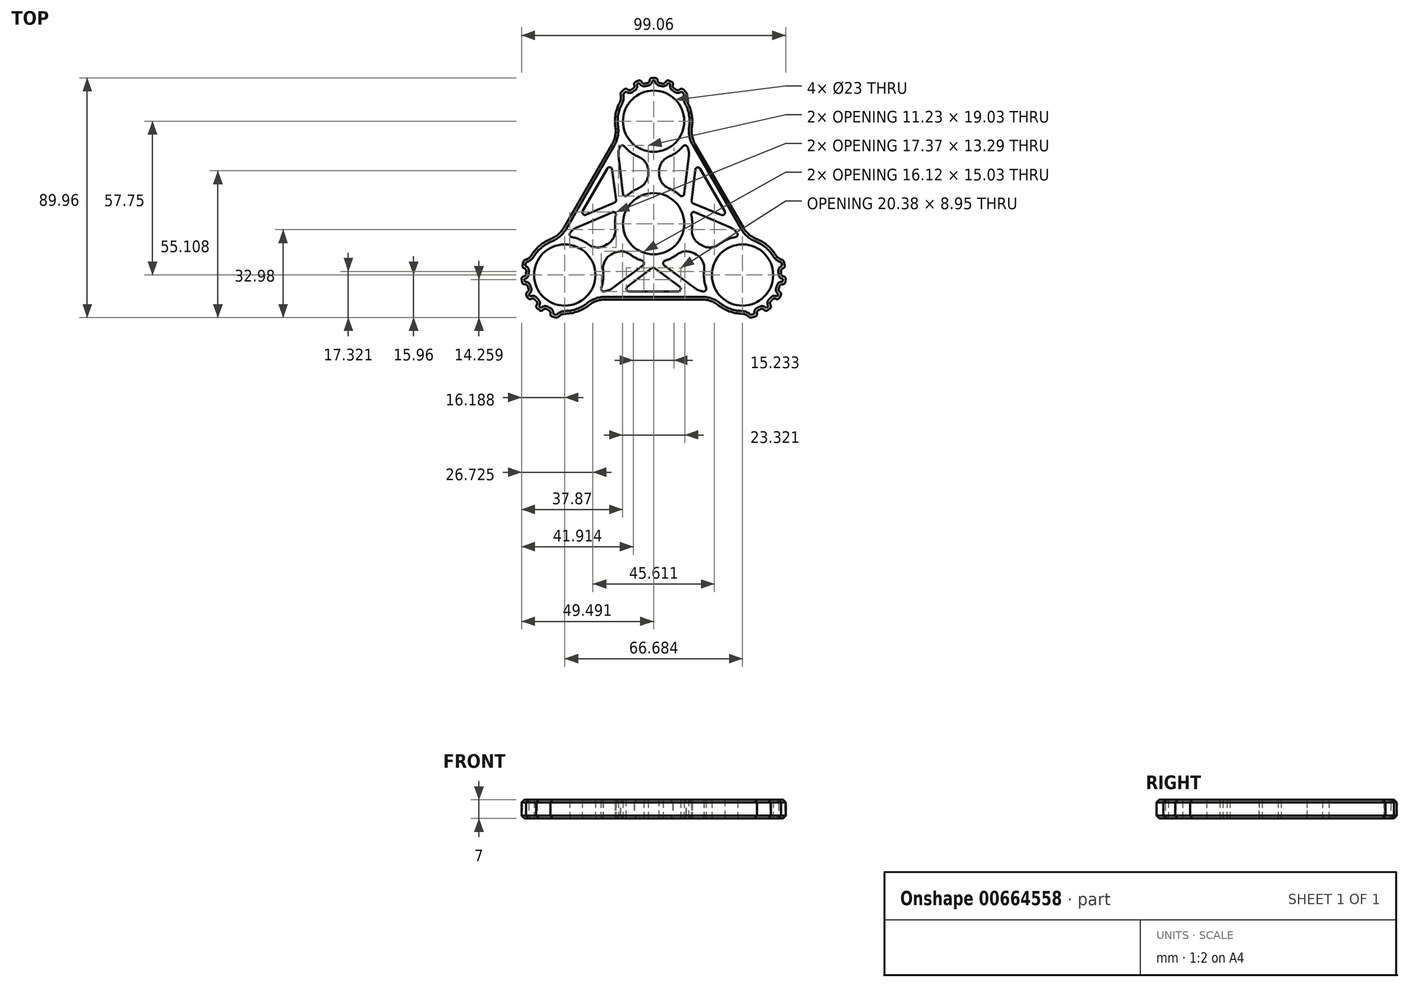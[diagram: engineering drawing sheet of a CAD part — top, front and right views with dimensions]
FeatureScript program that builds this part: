
annotation { "Feature Type Name" : "Feature", "Feature Type Description" : "" }
export const myFeature = defineFeature(function(context is Context, id is Id, definition is map)
    precondition{}
    {
        {
            var Q0;
            Q0=qCreatedBy(makeId("Top.planeOp"),FACE);
            var sketch = newSketch(context, id + "F0", { "sketchPlane" : qUnion([Q0])});
            skCircle(sketch, "E0", {"center": v(0, 0) * mm, "radius": 11.5 * mm});
            skArc(sketch, "E1.0", {"start": v(-2, 14.36) * mm, "mid": v(-7.13, 12.63) * mm, "end": v(-11.27, 9.13) * mm});
            skCircle(sketch, "E2", {"center": v(0, 38.5) * mm, "radius": 11.5 * mm});
            skArc(sketch, "E3.0", {"start": v(-11.26, 47.64) * mm, "mid": v(-14.31, 40.8) * mm, "end": v(-13.56, 33.37) * mm});
            skLineSegment(sketch, "E4", {"start": v(0, 11.5) * mm, "end": v(0, 27) * mm, "construction": true});
            skLineSegment(sketch, "E5.0", {"start": v(2, 14.36) * mm, "end": v(2, 24.14) * mm});
            skLineSegment(sketch, "E6.0", {"start": v(-2, 14.36) * mm, "end": v(-2, 24.14) * mm});
            skLineSegment(sketch, "E7", {"start": v(0, 53) * mm, "end": v(0, 55) * mm, "construction": true});
            skLineSegment(sketch, "E8.0", {"start": v(1.5, 52.92) * mm, "end": v(1.5, 54.75) * mm});
            skLineSegment(sketch, "E9.0", {"start": v(-1.5, 52.92) * mm, "end": v(-1.5, 54.75) * mm});
            skLineSegment(sketch, "E10", {"start": v(-1.5, 54.75) * mm, "end": v(1.5, 54.75) * mm});
            skLineSegment(sketch, "E11.1.0", {"start": v(4.83, 54.09) * mm, "end": v(7.6, 52.94) * mm});
            skLineSegment(sketch, "E11.1.1", {"start": v(4.13, 52.4) * mm, "end": v(4.83, 54.09) * mm});
            skLineSegment(sketch, "E11.1.2", {"start": v(6.9, 51.25) * mm, "end": v(7.6, 52.94) * mm});
            skLineSegment(sketch, "E11.2.0", {"start": v(10.43, 51.05) * mm, "end": v(12.55, 48.93) * mm});
            skLineSegment(sketch, "E11.2.1", {"start": v(9.14, 49.76) * mm, "end": v(10.43, 51.05) * mm});
            skLineSegment(sketch, "E11.2.2", {"start": v(11.26, 47.64) * mm, "end": v(12.55, 48.93) * mm});
            skLineSegment(sketch, "E11.anchor1", {"start": v(0, 38.5) * mm, "end": v(-1.5, 54.75) * mm, "construction": true});
            skLineSegment(sketch, "E11.anchor2", {"start": v(0, 38.5) * mm, "end": v(10.43, 51.05) * mm, "construction": true});
            skLineSegment(sketch, "E12.MirrorCS", {"start": v(-4.83, 54.09) * mm, "end": v(-7.6, 52.94) * mm});
            skLineSegment(sketch, "E13.MirrorCS", {"start": v(-4.13, 52.4) * mm, "end": v(-4.83, 54.09) * mm});
            skLineSegment(sketch, "E14.MirrorCS", {"start": v(-6.9, 51.25) * mm, "end": v(-7.6, 52.94) * mm});
            skLineSegment(sketch, "E15.MirrorCS", {"start": v(-9.14, 49.76) * mm, "end": v(-10.43, 51.05) * mm});
            skLineSegment(sketch, "E16.MirrorCS", {"start": v(-10.43, 51.05) * mm, "end": v(-12.55, 48.93) * mm});
            skLineSegment(sketch, "E17.MirrorCS", {"start": v(-11.26, 47.64) * mm, "end": v(-12.55, 48.93) * mm});
            skArc(sketch, "E18.trimOffspring", {"start": v(-6.9, 51.25) * mm, "mid": v(-8.06, 50.56) * mm, "end": v(-9.14, 49.76) * mm});
            skArc(sketch, "E19.trimOffspring", {"start": v(-1.33, 52.94) * mm, "mid": v(-2.75, 52.74) * mm, "end": v(-4.13, 52.4) * mm});
            skArc(sketch, "E20.trimOffspring", {"start": v(4.13, 52.4) * mm, "mid": v(2.83, 52.72) * mm, "end": v(1.5, 52.92) * mm});
            skArc(sketch, "E21.trimOffspring", {"start": v(9.27, 49.65) * mm, "mid": v(8.13, 50.5) * mm, "end": v(6.9, 51.25) * mm});
            skArc(sketch, "E22.trimOffspring", {"start": v(2, 24.14) * mm, "mid": v(7.6, 26.15) * mm, "end": v(11.9, 30.23) * mm});
            skLineSegment(sketch, "E23.1.0", {"start": v(-33.34, -19.25) * mm, "end": v(-46.66, -28.67) * mm, "construction": true});
            skPoint(sketch, "E23.1.1", {"position": v(-33.34, -19.25) * mm});
            skCircle(sketch, "E23.1.2", {"center": v(-33.34, -19.25) * mm, "radius": 11.5 * mm});
            skLineSegment(sketch, "E23.1.3", {"start": v(-9.96, -5.75) * mm, "end": v(-23.38, -13.5) * mm, "construction": true});
            skArc(sketch, "E23.1.4", {"start": v(-35.63, -33.57) * mm, "mid": v(-28.18, -32.8) * mm, "end": v(-22.12, -28.43) * mm});
            skLineSegment(sketch, "E23.1.5", {"start": v(-13.44, -5.45) * mm, "end": v(-21.9, -10.34) * mm});
            skLineSegment(sketch, "E23.1.6", {"start": v(-11.44, -8.91) * mm, "end": v(-19.9, -13.8) * mm});
            skLineSegment(sketch, "E23.1.7", {"start": v(-33.34, -19.25) * mm, "end": v(-49.43, -16.5) * mm, "construction": true});
            skArc(sketch, "E23.1.8", {"start": v(-21.9, -10.34) * mm, "mid": v(-26.44, -6.5) * mm, "end": v(-32.13, -4.8) * mm});
            skLineSegment(sketch, "E23.1.9", {"start": v(-40.93, -31.6) * mm, "end": v(-42.04, -33.06) * mm});
            skLineSegment(sketch, "E23.1.10", {"start": v(-35.63, -33.57) * mm, "end": v(-36.1, -35.33) * mm});
            skLineSegment(sketch, "E23.1.11", {"start": v(-49.43, -16.5) * mm, "end": v(-48.65, -13.6) * mm});
            skLineSegment(sketch, "E23.1.12", {"start": v(-47.84, -19.65) * mm, "end": v(-49.65, -19.88) * mm});
            skArc(sketch, "E23.1.13", {"start": v(-47.63, -16.8) * mm, "mid": v(-47.8, -18.22) * mm, "end": v(-47.84, -19.65) * mm});
            skLineSegment(sketch, "E23.1.14", {"start": v(-44.42, -31.23) * mm, "end": v(-42.04, -33.06) * mm});
            skLineSegment(sketch, "E23.1.15", {"start": v(-45.9, -26.5) * mm, "end": v(-47.63, -27.5) * mm, "construction": true});
            skLineSegment(sketch, "E23.1.16", {"start": v(-46.58, -25.16) * mm, "end": v(-48.16, -26.08) * mm});
            skLineSegment(sketch, "E23.1.17", {"start": v(-46.66, -28.67) * mm, "end": v(-48.16, -26.08) * mm});
            skLineSegment(sketch, "E23.1.18", {"start": v(-45.08, -27.76) * mm, "end": v(-46.66, -28.67) * mm});
            skLineSegment(sketch, "E23.1.19", {"start": v(-49.26, -22.86) * mm, "end": v(-49.65, -19.88) * mm});
            skLineSegment(sketch, "E23.1.20", {"start": v(-47.45, -22.62) * mm, "end": v(-49.26, -22.86) * mm});
            skArc(sketch, "E23.1.21", {"start": v(-47.45, -22.62) * mm, "mid": v(-47.07, -23.91) * mm, "end": v(-46.58, -25.16) * mm});
            skArc(sketch, "E23.1.22", {"start": v(-40.93, -31.6) * mm, "mid": v(-39.76, -32.25) * mm, "end": v(-38.52, -32.8) * mm});
            skLineSegment(sketch, "E23.1.23", {"start": v(-39, -34.56) * mm, "end": v(-36.1, -35.33) * mm});
            skLineSegment(sketch, "E23.1.24", {"start": v(-43.31, -29.78) * mm, "end": v(-44.42, -31.23) * mm});
            skLineSegment(sketch, "E23.1.25", {"start": v(-46.88, -14.07) * mm, "end": v(-48.65, -13.6) * mm});
            skArc(sketch, "E23.1.26", {"start": v(-45.18, -27.62) * mm, "mid": v(-44.3, -28.75) * mm, "end": v(-43.31, -29.78) * mm});
            skLineSegment(sketch, "E23.1.27", {"start": v(-38.52, -32.8) * mm, "end": v(-39, -34.56) * mm});
            skLineSegment(sketch, "E23.1.28", {"start": v(-47.66, -16.97) * mm, "end": v(-49.43, -16.5) * mm});
            skLineSegment(sketch, "E23.2.0", {"start": v(33.34, -19.25) * mm, "end": v(48.16, -26.08) * mm, "construction": true});
            skPoint(sketch, "E23.2.1", {"position": v(33.34, -19.25) * mm});
            skCircle(sketch, "E23.2.2", {"center": v(33.34, -19.25) * mm, "radius": 11.5 * mm});
            skLineSegment(sketch, "E23.2.3", {"start": v(9.96, -5.75) * mm, "end": v(23.38, -13.5) * mm, "construction": true});
            skArc(sketch, "E23.2.4", {"start": v(46.88, -14.07) * mm, "mid": v(42.5, -8) * mm, "end": v(35.68, -4.94) * mm});
            skLineSegment(sketch, "E23.2.5", {"start": v(11.44, -8.91) * mm, "end": v(19.9, -13.8) * mm});
            skLineSegment(sketch, "E23.2.6", {"start": v(13.44, -5.45) * mm, "end": v(21.9, -10.34) * mm});
            skLineSegment(sketch, "E23.2.7", {"start": v(33.34, -19.25) * mm, "end": v(39, -34.56) * mm, "construction": true});
            skArc(sketch, "E23.2.8", {"start": v(19.9, -13.8) * mm, "mid": v(18.85, -19.65) * mm, "end": v(20.22, -25.43) * mm});
            skLineSegment(sketch, "E23.2.9", {"start": v(47.84, -19.65) * mm, "end": v(49.65, -19.88) * mm});
            skLineSegment(sketch, "E23.2.10", {"start": v(46.88, -14.07) * mm, "end": v(48.65, -13.6) * mm});
            skLineSegment(sketch, "E23.2.11", {"start": v(39, -34.56) * mm, "end": v(36.1, -35.33) * mm});
            skLineSegment(sketch, "E23.2.12", {"start": v(40.93, -31.6) * mm, "end": v(42.04, -33.06) * mm});
            skArc(sketch, "E23.2.13", {"start": v(38.37, -32.85) * mm, "mid": v(39.68, -32.3) * mm, "end": v(40.93, -31.6) * mm});
            skLineSegment(sketch, "E23.2.14", {"start": v(49.26, -22.86) * mm, "end": v(49.65, -19.88) * mm});
            skLineSegment(sketch, "E23.2.15", {"start": v(45.9, -26.5) * mm, "end": v(47.63, -27.5) * mm, "construction": true});
            skLineSegment(sketch, "E23.2.16", {"start": v(45.08, -27.76) * mm, "end": v(46.66, -28.67) * mm});
            skLineSegment(sketch, "E23.2.17", {"start": v(48.16, -26.08) * mm, "end": v(46.66, -28.67) * mm});
            skLineSegment(sketch, "E23.2.18", {"start": v(46.58, -25.16) * mm, "end": v(48.16, -26.08) * mm});
            skLineSegment(sketch, "E23.2.19", {"start": v(44.42, -31.23) * mm, "end": v(42.04, -33.06) * mm});
            skLineSegment(sketch, "E23.2.20", {"start": v(43.31, -29.78) * mm, "end": v(44.42, -31.23) * mm});
            skArc(sketch, "E23.2.21", {"start": v(43.31, -29.78) * mm, "mid": v(44.24, -28.81) * mm, "end": v(45.08, -27.76) * mm});
            skArc(sketch, "E23.2.22", {"start": v(47.84, -19.65) * mm, "mid": v(47.81, -18.3) * mm, "end": v(47.66, -16.97) * mm});
            skLineSegment(sketch, "E23.2.23", {"start": v(49.43, -16.5) * mm, "end": v(48.65, -13.6) * mm});
            skLineSegment(sketch, "E23.2.24", {"start": v(47.45, -22.62) * mm, "end": v(49.26, -22.86) * mm});
            skLineSegment(sketch, "E23.2.25", {"start": v(35.63, -33.57) * mm, "end": v(36.1, -35.33) * mm});
            skArc(sketch, "E23.2.26", {"start": v(46.51, -25.32) * mm, "mid": v(47.05, -24) * mm, "end": v(47.45, -22.62) * mm});
            skLineSegment(sketch, "E23.2.27", {"start": v(47.66, -16.97) * mm, "end": v(49.43, -16.5) * mm});
            skLineSegment(sketch, "E23.2.28", {"start": v(38.52, -32.8) * mm, "end": v(39, -34.56) * mm});
            skArc(sketch, "E24.trimOffspring", {"start": v(13.44, -5.45) * mm, "mid": v(14.5, -0.14) * mm, "end": v(13.54, 5.2) * mm});
            skArc(sketch, "E25.trimOffspring", {"start": v(-11.44, -8.91) * mm, "mid": v(-7.37, -12.49) * mm, "end": v(-2.27, -14.32) * mm});
            skLineSegment(sketch, "E26", {"start": v(-13.56, 33.37) * mm, "end": v(-35.68, -4.94) * mm});
            skLineSegment(sketch, "E27.0", {"start": v(-11.9, 30.23) * mm, "end": v(-13.42, 27.6) * mm});
            skArc(sketch, "E28.trimOffspring", {"start": v(-11.9, 30.23) * mm, "mid": v(-7.6, 26.15) * mm, "end": v(-2, 24.14) * mm});
            skArc(sketch, "E29.trimOffspring", {"start": v(-35.68, -4.94) * mm, "mid": v(-42.5, -8) * mm, "end": v(-46.88, -14.07) * mm});
            skLineSegment(sketch, "E30", {"start": v(-12.56, 7.25) * mm, "end": v(-29.36, 0) * mm, "construction": true});
            skLineSegment(sketch, "E31", {"start": v(-12.56, 7.25) * mm, "end": v(-22.02, 12.71) * mm, "construction": true});
            skLineSegment(sketch, "E32.0", {"start": v(-13.95, 8.28) * mm, "end": v(-28.1, 2.18) * mm});
            skLineSegment(sketch, "E33.0", {"start": v(-13.54, 5.2) * mm, "end": v(-30.62, -2.18) * mm});
            skLineSegment(sketch, "E34.trimOffspring", {"start": v(-30.62, -2.18) * mm, "end": v(-32.13, -4.8) * mm});
            skArc(sketch, "E35.trimOffspring", {"start": v(-13.54, 5.2) * mm, "mid": v(-14.5, -0.14) * mm, "end": v(-13.44, -5.45) * mm});
            skLineSegment(sketch, "E36.MirrorCS", {"start": v(-11.27, 9.13) * mm, "end": v(-13.42, 27.6) * mm});
            skLineSegment(sketch, "E37.trimOffspring", {"start": v(-15.94, 23.25) * mm, "end": v(-28.1, 2.18) * mm});
            skPoint(sketch, "E38.orphan", {"position": v(-10.85, 9.62) * mm});
            skLineSegment(sketch, "E39.trimOffspring", {"start": v(-13.95, 8.28) * mm, "end": v(-15.94, 23.25) * mm});
            skPoint(sketch, "E40.MirrorCS.start.orphan", {"position": v(-13.76, 4.58) * mm});
            skLineSegment(sketch, "E41.1.0", {"start": v(-22.12, -28.43) * mm, "end": v(22.12, -28.43) * mm});
            skLineSegment(sketch, "E41.1.1", {"start": v(-0.2, -16.22) * mm, "end": v(-12.17, -25.43) * mm});
            skLineSegment(sketch, "E41.1.2", {"start": v(0, -14.5) * mm, "end": v(0, -25.43) * mm, "construction": true});
            skLineSegment(sketch, "E41.1.3", {"start": v(-12.17, -25.43) * mm, "end": v(12.17, -25.43) * mm});
            skLineSegment(sketch, "E41.1.4", {"start": v(-2.27, -14.32) * mm, "end": v(-17.2, -25.43) * mm});
            skLineSegment(sketch, "E41.1.5", {"start": v(17.2, -25.43) * mm, "end": v(20.22, -25.43) * mm});
            skLineSegment(sketch, "E41.1.6", {"start": v(2.27, -14.32) * mm, "end": v(17.2, -25.43) * mm});
            skLineSegment(sketch, "E41.1.7", {"start": v(-0.2, -16.22) * mm, "end": v(12.17, -25.43) * mm});
            skLineSegment(sketch, "E41.1.8", {"start": v(0, -14.5) * mm, "end": v(14.68, -25.43) * mm, "construction": true});
            skLineSegment(sketch, "E41.1.9", {"start": v(-20.22, -25.43) * mm, "end": v(-17.2, -25.43) * mm});
            skLineSegment(sketch, "E41.2.0", {"start": v(35.68, -4.94) * mm, "end": v(13.56, 33.37) * mm});
            skLineSegment(sketch, "E41.2.1", {"start": v(14.15, 7.94) * mm, "end": v(28.1, 2.18) * mm});
            skLineSegment(sketch, "E41.2.2", {"start": v(12.56, 7.25) * mm, "end": v(22.02, 12.71) * mm, "construction": true});
            skLineSegment(sketch, "E41.2.3", {"start": v(28.1, 2.18) * mm, "end": v(15.94, 23.25) * mm});
            skLineSegment(sketch, "E41.2.4", {"start": v(13.54, 5.2) * mm, "end": v(30.62, -2.18) * mm});
            skLineSegment(sketch, "E41.2.5", {"start": v(13.42, 27.6) * mm, "end": v(11.9, 30.23) * mm});
            skLineSegment(sketch, "E41.2.6", {"start": v(11.27, 9.13) * mm, "end": v(13.42, 27.6) * mm});
            skLineSegment(sketch, "E41.2.7", {"start": v(14.15, 7.94) * mm, "end": v(15.94, 23.25) * mm});
            skLineSegment(sketch, "E41.2.8", {"start": v(12.56, 7.25) * mm, "end": v(14.68, 25.43) * mm, "construction": true});
            skLineSegment(sketch, "E41.2.9", {"start": v(32.13, -4.8) * mm, "end": v(30.62, -2.18) * mm});
            skArc(sketch, "E42.trimOffspring", {"start": v(13.56, 33.37) * mm, "mid": v(14.31, 40.8) * mm, "end": v(11.26, 47.64) * mm});
            skArc(sketch, "E43.trimOffspring", {"start": v(32.13, -4.8) * mm, "mid": v(26.44, -6.5) * mm, "end": v(21.9, -10.34) * mm});
            skArc(sketch, "E44.trimOffspring", {"start": v(11.27, 9.13) * mm, "mid": v(7.13, 12.63) * mm, "end": v(2, 14.36) * mm});
            skArc(sketch, "E45.trimOffspring", {"start": v(2.27, -14.32) * mm, "mid": v(7.37, -12.49) * mm, "end": v(11.44, -8.91) * mm});
            skArc(sketch, "E46.trimOffspring", {"start": v(22.12, -28.43) * mm, "mid": v(28.18, -32.8) * mm, "end": v(35.63, -33.57) * mm});
            skArc(sketch, "E47.trimOffspring", {"start": v(-20.22, -25.43) * mm, "mid": v(-18.85, -19.65) * mm, "end": v(-19.9, -13.8) * mm});
            skSolve(sketch);
        }
        {
            var Q0;
            Q0=qSketchRegion(id+"F0",true);
            extrude(context, id + "F1", {"entities" : qUnion([Q0]), "depth" : 7 * mm});
        }
        {
            var Q0;
            Q0=makeQuery(id+"F1.opExtrude","SWEPT_EDGE",EDGE,{"disambiguationData":[OSD([sQuery(id+"F0.wireOp",EDGE,"E1.0"),sQuery(id+"F0.wireOp",EDGE,"E6.0")])]});
            var Q1;
            Q1=makeQuery(id+"F1.opExtrude","SWEPT_EDGE",EDGE,{"disambiguationData":[OSD([sQuery(id+"F0.wireOp",EDGE,"E5.0"),sQuery(id+"F0.wireOp",EDGE,"E44.trimOffspring")])]});
            var Q2;
            Q2=makeQuery(id+"F1.opExtrude","SWEPT_EDGE",EDGE,{"disambiguationData":[OSD([sQuery(id+"F0.wireOp",EDGE,"E5.0"),sQuery(id+"F0.wireOp",EDGE,"E22.trimOffspring")])]});
            var Q3;
            Q3=makeQuery(id+"F1.opExtrude","SWEPT_EDGE",EDGE,{"disambiguationData":[OSD([sQuery(id+"F0.wireOp",EDGE,"E6.0"),sQuery(id+"F0.wireOp",EDGE,"E28.trimOffspring")])]});
            var Q4;
            Q4=makeQuery(id+"F1.opExtrude","SWEPT_EDGE",EDGE,{"disambiguationData":[OSD([sQuery(id+"F0.wireOp",EDGE,"E23.1.5"),sQuery(id+"F0.wireOp",EDGE,"E35.trimOffspring")])]});
            var Q5;
            Q5=makeQuery(id+"F1.opExtrude","SWEPT_EDGE",EDGE,{"disambiguationData":[OSD([sQuery(id+"F0.wireOp",EDGE,"E23.2.5"),sQuery(id+"F0.wireOp",EDGE,"E23.2.8")])]});
            var Q6;
            Q6=makeQuery(id+"F1.opExtrude","SWEPT_EDGE",EDGE,{"disambiguationData":[OSD([sQuery(id+"F0.wireOp",EDGE,"E23.1.6"),sQuery(id+"F0.wireOp",EDGE,"E47.trimOffspring")])]});
            var Q7;
            Q7=makeQuery(id+"F1.opExtrude","SWEPT_EDGE",EDGE,{"disambiguationData":[OSD([sQuery(id+"F0.wireOp",EDGE,"E23.1.6"),sQuery(id+"F0.wireOp",EDGE,"E25.trimOffspring")])]});
            var Q8;
            Q8=makeQuery(id+"F1.opExtrude","SWEPT_EDGE",EDGE,{"disambiguationData":[OSD([sQuery(id+"F0.wireOp",EDGE,"E23.1.5"),sQuery(id+"F0.wireOp",EDGE,"E23.1.8")])]});
            var Q9;
            Q9=makeQuery(id+"F1.opExtrude","SWEPT_EDGE",EDGE,{"disambiguationData":[OSD([sQuery(id+"F0.wireOp",EDGE,"E23.2.6"),sQuery(id+"F0.wireOp",EDGE,"E43.trimOffspring")])]});
            var Q10;
            Q10=makeQuery(id+"F1.opExtrude","SWEPT_EDGE",EDGE,{"disambiguationData":[OSD([sQuery(id+"F0.wireOp",EDGE,"E23.2.5"),sQuery(id+"F0.wireOp",EDGE,"E45.trimOffspring")])]});
            var Q11;
            Q11=makeQuery(id+"F1.opExtrude","SWEPT_EDGE",EDGE,{"disambiguationData":[OSD([sQuery(id+"F0.wireOp",EDGE,"E23.2.6"),sQuery(id+"F0.wireOp",EDGE,"E24.trimOffspring")])]});
            var Q12;
            Q12=makeQuery(id+"F1.opExtrude","SWEPT_EDGE",EDGE,{"disambiguationData":[OSD([sQuery(id+"F0.wireOp",EDGE,"E33.0"),sQuery(id+"F0.wireOp",EDGE,"E34.trimOffspring")])]});
            var Q13;
            Q13=makeQuery(id+"F1.opExtrude","SWEPT_EDGE",EDGE,{"disambiguationData":[OSD([sQuery(id+"F0.wireOp",EDGE,"E41.1.4"),sQuery(id+"F0.wireOp",EDGE,"E41.1.9")])]});
            var Q14;
            Q14=makeQuery(id+"F1.opExtrude","SWEPT_EDGE",EDGE,{"disambiguationData":[OSD([sQuery(id+"F0.wireOp",EDGE,"E41.1.5"),sQuery(id+"F0.wireOp",EDGE,"E41.1.6")])]});
            var Q15;
            Q15=makeQuery(id+"F1.opExtrude","SWEPT_EDGE",EDGE,{"disambiguationData":[OSD([sQuery(id+"F0.wireOp",EDGE,"E41.2.5"),sQuery(id+"F0.wireOp",EDGE,"E41.2.6")])]});
            var Q16;
            Q16=makeQuery(id+"F1.opExtrude","SWEPT_EDGE",EDGE,{"disambiguationData":[OSD([sQuery(id+"F0.wireOp",EDGE,"E41.2.4"),sQuery(id+"F0.wireOp",EDGE,"E41.2.9")])]});
            var Q17;
            Q17=makeQuery(id+"F1.opExtrude","SWEPT_EDGE",EDGE,{"disambiguationData":[OSD([sQuery(id+"F0.wireOp",EDGE,"E27.0"),sQuery(id+"F0.wireOp",EDGE,"E36.MirrorCS")])]});
            fillet(context, id + "F2", {"entities" : qUnion([Q0, Q1, Q2, Q3, Q4, Q5, Q6, Q7, Q8, Q9, Q10, Q11, Q12, Q13, Q14, Q15, Q16, Q17]), "radius" : 6 * mm, "tangentPropagation" : true, "allowEdgeOverflow" : false});
        }
        {
            var Q0;
            Q0=makeQuery(id+"F1.opExtrude","SWEPT_EDGE",EDGE,{"disambiguationData":[OSD([sQuery(id+"F0.wireOp",EDGE,"E1.0"),sQuery(id+"F0.wireOp",EDGE,"E36.MirrorCS")])]});
            var Q1;
            Q1=makeQuery(id+"F1.opExtrude","SWEPT_EDGE",EDGE,{"disambiguationData":[OSD([sQuery(id+"F0.wireOp",EDGE,"E33.0"),sQuery(id+"F0.wireOp",EDGE,"E35.trimOffspring")])]});
            var Q2;
            Q2=makeQuery(id+"F1.opExtrude","SWEPT_EDGE",EDGE,{"disambiguationData":[OSD([sQuery(id+"F0.wireOp",EDGE,"E25.trimOffspring"),sQuery(id+"F0.wireOp",EDGE,"E41.1.4")])]});
            var Q3;
            Q3=makeQuery(id+"F1.opExtrude","SWEPT_EDGE",EDGE,{"disambiguationData":[OSD([sQuery(id+"F0.wireOp",EDGE,"E41.1.6"),sQuery(id+"F0.wireOp",EDGE,"E45.trimOffspring")])]});
            var Q4;
            Q4=makeQuery(id+"F1.opExtrude","SWEPT_EDGE",EDGE,{"disambiguationData":[OSD([sQuery(id+"F0.wireOp",EDGE,"E24.trimOffspring"),sQuery(id+"F0.wireOp",EDGE,"E41.2.4")])]});
            var Q5;
            Q5=makeQuery(id+"F1.opExtrude","SWEPT_EDGE",EDGE,{"disambiguationData":[OSD([sQuery(id+"F0.wireOp",EDGE,"E41.2.6"),sQuery(id+"F0.wireOp",EDGE,"E44.trimOffspring")])]});
            var Q6;
            Q6=makeQuery(id+"F1.opExtrude","SWEPT_EDGE",EDGE,{"disambiguationData":[OSD([sQuery(id+"F0.wireOp",EDGE,"E41.2.9"),sQuery(id+"F0.wireOp",EDGE,"E43.trimOffspring")])]});
            var Q7;
            Q7=makeQuery(id+"F1.opExtrude","SWEPT_EDGE",EDGE,{"disambiguationData":[OSD([sQuery(id+"F0.wireOp",EDGE,"E23.2.8"),sQuery(id+"F0.wireOp",EDGE,"E41.1.5")])]});
            var Q8;
            Q8=makeQuery(id+"F1.opExtrude","SWEPT_EDGE",EDGE,{"disambiguationData":[OSD([sQuery(id+"F0.wireOp",EDGE,"E41.1.9"),sQuery(id+"F0.wireOp",EDGE,"E47.trimOffspring")])]});
            var Q9;
            Q9=makeQuery(id+"F1.opExtrude","SWEPT_EDGE",EDGE,{"disambiguationData":[OSD([sQuery(id+"F0.wireOp",EDGE,"E23.1.8"),sQuery(id+"F0.wireOp",EDGE,"E34.trimOffspring")])]});
            var Q10;
            Q10=makeQuery(id+"F1.opExtrude","SWEPT_EDGE",EDGE,{"disambiguationData":[OSD([sQuery(id+"F0.wireOp",EDGE,"E22.trimOffspring"),sQuery(id+"F0.wireOp",EDGE,"E41.2.5")])]});
            var Q11;
            Q11=makeQuery(id+"F1.opExtrude","SWEPT_EDGE",EDGE,{"disambiguationData":[OSD([sQuery(id+"F0.wireOp",EDGE,"E27.0"),sQuery(id+"F0.wireOp",EDGE,"E28.trimOffspring")])]});
            var Q12;
            Q12=makeQuery(id+"F1.opExtrude","SWEPT_EDGE",EDGE,{"disambiguationData":[OSD([sQuery(id+"F0.wireOp",EDGE,"E37.trimOffspring"),sQuery(id+"F0.wireOp",EDGE,"E39.trimOffspring")])]});
            var Q13;
            Q13=makeQuery(id+"F1.opExtrude","SWEPT_EDGE",EDGE,{"disambiguationData":[OSD([sQuery(id+"F0.wireOp",EDGE,"E32.0"),sQuery(id+"F0.wireOp",EDGE,"E37.trimOffspring")])]});
            var Q14;
            Q14=makeQuery(id+"F1.opExtrude","SWEPT_EDGE",EDGE,{"disambiguationData":[OSD([sQuery(id+"F0.wireOp",EDGE,"E41.2.1"),sQuery(id+"F0.wireOp",EDGE,"E41.2.3")])]});
            var Q15;
            Q15=makeQuery(id+"F1.opExtrude","SWEPT_EDGE",EDGE,{"disambiguationData":[OSD([sQuery(id+"F0.wireOp",EDGE,"E41.2.3"),sQuery(id+"F0.wireOp",EDGE,"E41.2.7")])]});
            var Q16;
            Q16=makeQuery(id+"F1.opExtrude","SWEPT_EDGE",EDGE,{"disambiguationData":[OSD([sQuery(id+"F0.wireOp",EDGE,"E41.1.3"),sQuery(id+"F0.wireOp",EDGE,"E41.1.7")])]});
            var Q17;
            Q17=makeQuery(id+"F1.opExtrude","SWEPT_EDGE",EDGE,{"disambiguationData":[OSD([sQuery(id+"F0.wireOp",EDGE,"E41.1.1"),sQuery(id+"F0.wireOp",EDGE,"E41.1.3")])]});
            var Q18;
            Q18=makeQuery(id+"F1.opExtrude","SWEPT_EDGE",EDGE,{"disambiguationData":[OSD([sQuery(id+"F0.wireOp",EDGE,"E32.0"),sQuery(id+"F0.wireOp",EDGE,"E39.trimOffspring")])]});
            var Q19;
            Q19=makeQuery(id+"F1.opExtrude","SWEPT_EDGE",EDGE,{"disambiguationData":[OSD([sQuery(id+"F0.wireOp",EDGE,"E41.1.1"),sQuery(id+"F0.wireOp",EDGE,"E41.1.7")])]});
            var Q20;
            Q20=makeQuery(id+"F1.opExtrude","SWEPT_EDGE",EDGE,{"disambiguationData":[OSD([sQuery(id+"F0.wireOp",EDGE,"E41.2.1"),sQuery(id+"F0.wireOp",EDGE,"E41.2.7")])]});
            fillet(context, id + "F3", {"entities" : qUnion([Q0, Q1, Q2, Q3, Q4, Q5, Q6, Q7, Q8, Q9, Q10, Q11, Q12, Q13, Q14, Q15, Q16, Q17, Q18, Q19, Q20]), "radius" : 1 * mm, "tangentPropagation" : true, "allowEdgeOverflow" : false});
        }
        {
            var Q0;
            Q0=makeQuery(id+"F1.opExtrude","SWEPT_EDGE",EDGE,{"disambiguationData":[OSD([sQuery(id+"F0.wireOp",EDGE,"E3.0"),sQuery(id+"F0.wireOp",EDGE,"E26")])]});
            var Q1;
            Q1=makeQuery(id+"F1.opExtrude","SWEPT_EDGE",EDGE,{"disambiguationData":[OSD([sQuery(id+"F0.wireOp",EDGE,"E41.2.0"),sQuery(id+"F0.wireOp",EDGE,"E42.trimOffspring")])]});
            var Q2;
            Q2=makeQuery(id+"F1.opExtrude","SWEPT_EDGE",EDGE,{"disambiguationData":[OSD([sQuery(id+"F0.wireOp",EDGE,"E26"),sQuery(id+"F0.wireOp",EDGE,"E29.trimOffspring")])]});
            var Q3;
            Q3=makeQuery(id+"F1.opExtrude","SWEPT_EDGE",EDGE,{"disambiguationData":[OSD([sQuery(id+"F0.wireOp",EDGE,"E23.1.4"),sQuery(id+"F0.wireOp",EDGE,"E41.1.0")])]});
            var Q4;
            Q4=makeQuery(id+"F1.opExtrude","SWEPT_EDGE",EDGE,{"disambiguationData":[OSD([sQuery(id+"F0.wireOp",EDGE,"E41.1.0"),sQuery(id+"F0.wireOp",EDGE,"E46.trimOffspring")])]});
            var Q5;
            Q5=makeQuery(id+"F1.opExtrude","SWEPT_EDGE",EDGE,{"disambiguationData":[OSD([sQuery(id+"F0.wireOp",EDGE,"E23.2.4"),sQuery(id+"F0.wireOp",EDGE,"E41.2.0")])]});
            fillet(context, id + "F4", {"entities" : qUnion([Q0, Q1, Q2, Q3, Q4, Q5]), "radius" : 10 * mm, "tangentPropagation" : true, "allowEdgeOverflow" : false});
        }
        {
            var Q0;
            Q0=makeQuery(id+"F1.opExtrude","SWEPT_EDGE",EDGE,{"disambiguationData":[OSD([sQuery(id+"F0.wireOp",EDGE,"E3.0"),sQuery(id+"F0.wireOp",EDGE,"E17.MirrorCS")])]});
            var Q1;
            Q1=makeQuery(id+"F1.opExtrude","SWEPT_EDGE",EDGE,{"disambiguationData":[OSD([sQuery(id+"F0.wireOp",EDGE,"E11.2.2"),sQuery(id+"F0.wireOp",EDGE,"E42.trimOffspring")])]});
            var Q2;
            Q2=makeQuery(id+"F1.opExtrude","SWEPT_EDGE",EDGE,{"disambiguationData":[OSD([sQuery(id+"F0.wireOp",EDGE,"E23.1.25"),sQuery(id+"F0.wireOp",EDGE,"E29.trimOffspring")])]});
            var Q3;
            Q3=makeQuery(id+"F1.opExtrude","SWEPT_EDGE",EDGE,{"disambiguationData":[OSD([sQuery(id+"F0.wireOp",EDGE,"E23.1.4"),sQuery(id+"F0.wireOp",EDGE,"E23.1.10")])]});
            var Q4;
            Q4=makeQuery(id+"F1.opExtrude","SWEPT_EDGE",EDGE,{"disambiguationData":[OSD([sQuery(id+"F0.wireOp",EDGE,"E23.2.25"),sQuery(id+"F0.wireOp",EDGE,"E46.trimOffspring")])]});
            var Q5;
            Q5=makeQuery(id+"F1.opExtrude","SWEPT_EDGE",EDGE,{"disambiguationData":[OSD([sQuery(id+"F0.wireOp",EDGE,"E23.2.4"),sQuery(id+"F0.wireOp",EDGE,"E23.2.10")])]});
            fillet(context, id + "F5", {"entities" : qUnion([Q0, Q1, Q2, Q3, Q4, Q5]), "radius" : 4 * mm, "tangentPropagation" : true, "allowEdgeOverflow" : false});
        }
        {
            var Q0;
            Q0=makeQuery(id+"F1.opExtrude","SWEPT_EDGE",EDGE,{"disambiguationData":[OSD([sQuery(id+"F0.wireOp",EDGE,"E15.MirrorCS"),sQuery(id+"F0.wireOp",EDGE,"E18.trimOffspring")])]});
            var Q1;
            Q1=makeQuery(id+"F1.opExtrude","SWEPT_EDGE",EDGE,{"disambiguationData":[OSD([sQuery(id+"F0.wireOp",EDGE,"E14.MirrorCS"),sQuery(id+"F0.wireOp",EDGE,"E18.trimOffspring")])]});
            var Q2;
            Q2=makeQuery(id+"F1.opExtrude","SWEPT_EDGE",EDGE,{"disambiguationData":[OSD([sQuery(id+"F0.wireOp",EDGE,"E13.MirrorCS"),sQuery(id+"F0.wireOp",EDGE,"E19.trimOffspring")])]});
            var Q3;
            Q3=makeQuery(id+"F1.opExtrude","SWEPT_EDGE",EDGE,{"disambiguationData":[OSD([sQuery(id+"F0.wireOp",EDGE,"E9.0"),sQuery(id+"F0.wireOp",EDGE,"E19.trimOffspring")])]});
            var Q4;
            Q4=makeQuery(id+"F1.opExtrude","SWEPT_EDGE",EDGE,{"disambiguationData":[OSD([sQuery(id+"F0.wireOp",EDGE,"E8.0"),sQuery(id+"F0.wireOp",EDGE,"E20.trimOffspring")])]});
            var Q5;
            Q5=makeQuery(id+"F1.opExtrude","SWEPT_EDGE",EDGE,{"disambiguationData":[OSD([sQuery(id+"F0.wireOp",EDGE,"E11.1.2"),sQuery(id+"F0.wireOp",EDGE,"E21.trimOffspring")])]});
            var Q6;
            Q6=makeQuery(id+"F1.opExtrude","SWEPT_EDGE",EDGE,{"disambiguationData":[OSD([sQuery(id+"F0.wireOp",EDGE,"E11.1.1"),sQuery(id+"F0.wireOp",EDGE,"E20.trimOffspring")])]});
            var Q7;
            Q7=makeQuery(id+"F1.opExtrude","SWEPT_EDGE",EDGE,{"disambiguationData":[OSD([sQuery(id+"F0.wireOp",EDGE,"E11.2.1"),sQuery(id+"F0.wireOp",EDGE,"E21.trimOffspring")])]});
            var Q8;
            Q8=makeQuery(id+"F1.opExtrude","SWEPT_EDGE",EDGE,{"disambiguationData":[OSD([sQuery(id+"F0.wireOp",EDGE,"E23.1.13"),sQuery(id+"F0.wireOp",EDGE,"E23.1.28")])]});
            var Q9;
            Q9=makeQuery(id+"F1.opExtrude","SWEPT_EDGE",EDGE,{"disambiguationData":[OSD([sQuery(id+"F0.wireOp",EDGE,"E23.1.20"),sQuery(id+"F0.wireOp",EDGE,"E23.1.21")])]});
            var Q10;
            Q10=makeQuery(id+"F1.opExtrude","SWEPT_EDGE",EDGE,{"disambiguationData":[OSD([sQuery(id+"F0.wireOp",EDGE,"E23.1.9"),sQuery(id+"F0.wireOp",EDGE,"E23.1.22")])]});
            var Q11;
            Q11=makeQuery(id+"F1.opExtrude","SWEPT_EDGE",EDGE,{"disambiguationData":[OSD([sQuery(id+"F0.wireOp",EDGE,"E23.1.18"),sQuery(id+"F0.wireOp",EDGE,"E23.1.26")])]});
            var Q12;
            Q12=makeQuery(id+"F1.opExtrude","SWEPT_EDGE",EDGE,{"disambiguationData":[OSD([sQuery(id+"F0.wireOp",EDGE,"E23.1.12"),sQuery(id+"F0.wireOp",EDGE,"E23.1.13")])]});
            var Q13;
            Q13=makeQuery(id+"F1.opExtrude","SWEPT_EDGE",EDGE,{"disambiguationData":[OSD([sQuery(id+"F0.wireOp",EDGE,"E23.1.16"),sQuery(id+"F0.wireOp",EDGE,"E23.1.21")])]});
            var Q14;
            Q14=makeQuery(id+"F1.opExtrude","SWEPT_EDGE",EDGE,{"disambiguationData":[OSD([sQuery(id+"F0.wireOp",EDGE,"E23.1.24"),sQuery(id+"F0.wireOp",EDGE,"E23.1.26")])]});
            var Q15;
            Q15=makeQuery(id+"F1.opExtrude","SWEPT_EDGE",EDGE,{"disambiguationData":[OSD([sQuery(id+"F0.wireOp",EDGE,"E23.1.22"),sQuery(id+"F0.wireOp",EDGE,"E23.1.27")])]});
            var Q16;
            Q16=makeQuery(id+"F1.opExtrude","SWEPT_EDGE",EDGE,{"disambiguationData":[OSD([sQuery(id+"F0.wireOp",EDGE,"E23.2.22"),sQuery(id+"F0.wireOp",EDGE,"E23.2.27")])]});
            var Q17;
            Q17=makeQuery(id+"F1.opExtrude","SWEPT_EDGE",EDGE,{"disambiguationData":[OSD([sQuery(id+"F0.wireOp",EDGE,"E23.2.24"),sQuery(id+"F0.wireOp",EDGE,"E23.2.26")])]});
            var Q18;
            Q18=makeQuery(id+"F1.opExtrude","SWEPT_EDGE",EDGE,{"disambiguationData":[OSD([sQuery(id+"F0.wireOp",EDGE,"E23.2.16"),sQuery(id+"F0.wireOp",EDGE,"E23.2.21")])]});
            var Q19;
            Q19=makeQuery(id+"F1.opExtrude","SWEPT_EDGE",EDGE,{"disambiguationData":[OSD([sQuery(id+"F0.wireOp",EDGE,"E23.2.12"),sQuery(id+"F0.wireOp",EDGE,"E23.2.13")])]});
            var Q20;
            Q20=makeQuery(id+"F1.opExtrude","SWEPT_EDGE",EDGE,{"disambiguationData":[OSD([sQuery(id+"F0.wireOp",EDGE,"E23.2.13"),sQuery(id+"F0.wireOp",EDGE,"E23.2.28")])]});
            var Q21;
            Q21=makeQuery(id+"F1.opExtrude","SWEPT_EDGE",EDGE,{"disambiguationData":[OSD([sQuery(id+"F0.wireOp",EDGE,"E23.2.20"),sQuery(id+"F0.wireOp",EDGE,"E23.2.21")])]});
            var Q22;
            Q22=makeQuery(id+"F1.opExtrude","SWEPT_EDGE",EDGE,{"disambiguationData":[OSD([sQuery(id+"F0.wireOp",EDGE,"E23.2.18"),sQuery(id+"F0.wireOp",EDGE,"E23.2.26")])]});
            var Q23;
            Q23=makeQuery(id+"F1.opExtrude","SWEPT_EDGE",EDGE,{"disambiguationData":[OSD([sQuery(id+"F0.wireOp",EDGE,"E23.2.9"),sQuery(id+"F0.wireOp",EDGE,"E23.2.22")])]});
            fillet(context, id + "F6", {"entities" : qUnion([Q0, Q1, Q2, Q3, Q4, Q5, Q6, Q7, Q8, Q9, Q10, Q11, Q12, Q13, Q14, Q15, Q16, Q17, Q18, Q19, Q20, Q21, Q22, Q23]), "radius" : 1 * mm, "tangentPropagation" : true, "allowEdgeOverflow" : false});
        }
        {
            var Q0;
            Q0=makeQuery(id+"F1.opExtrude","SWEPT_EDGE",EDGE,{"disambiguationData":[OSD([sQuery(id+"F0.wireOp",EDGE,"E12.MirrorCS"),sQuery(id+"F0.wireOp",EDGE,"E14.MirrorCS")])]});
            var Q1;
            Q1=makeQuery(id+"F1.opExtrude","SWEPT_EDGE",EDGE,{"disambiguationData":[OSD([sQuery(id+"F0.wireOp",EDGE,"E12.MirrorCS"),sQuery(id+"F0.wireOp",EDGE,"E13.MirrorCS")])]});
            var Q2;
            Q2=makeQuery(id+"F5.opFillet","BLEND_EDGE",EDGE,{"blendedFrom":[makeQuery(id+"F1.opExtrude","SWEPT_EDGE",EDGE,{"disambiguationData":[OSD([sQuery(id+"F0.wireOp",EDGE,"E3.0"),sQuery(id+"F0.wireOp",EDGE,"E17.MirrorCS")])]}),makeQuery(id+"F1.opExtrude","SWEPT_FACE",FACE,{"disambiguationData":[OSD([sQuery(id+"F0.wireOp",EDGE,"E16.MirrorCS")])]})],"blendedInto":[makeQuery(id+"F1.opExtrude","SWEPT_FACE",FACE,{"disambiguationData":[OSD([sQuery(id+"F0.wireOp",EDGE,"E16.MirrorCS")])]})]});
            var Q3;
            Q3=makeQuery(id+"F1.opExtrude","SWEPT_EDGE",EDGE,{"disambiguationData":[OSD([sQuery(id+"F0.wireOp",EDGE,"E15.MirrorCS"),sQuery(id+"F0.wireOp",EDGE,"E16.MirrorCS")])]});
            var Q4;
            Q4=makeQuery(id+"F1.opExtrude","SWEPT_EDGE",EDGE,{"disambiguationData":[OSD([sQuery(id+"F0.wireOp",EDGE,"E9.0"),sQuery(id+"F0.wireOp",EDGE,"E10")])]});
            var Q5;
            Q5=makeQuery(id+"F1.opExtrude","SWEPT_EDGE",EDGE,{"disambiguationData":[OSD([sQuery(id+"F0.wireOp",EDGE,"E8.0"),sQuery(id+"F0.wireOp",EDGE,"E10")])]});
            var Q6;
            Q6=makeQuery(id+"F1.opExtrude","SWEPT_EDGE",EDGE,{"disambiguationData":[OSD([sQuery(id+"F0.wireOp",EDGE,"E11.1.0"),sQuery(id+"F0.wireOp",EDGE,"E11.1.1")])]});
            var Q7;
            Q7=makeQuery(id+"F1.opExtrude","SWEPT_EDGE",EDGE,{"disambiguationData":[OSD([sQuery(id+"F0.wireOp",EDGE,"E11.1.0"),sQuery(id+"F0.wireOp",EDGE,"E11.1.2")])]});
            var Q8;
            Q8=makeQuery(id+"F1.opExtrude","SWEPT_EDGE",EDGE,{"disambiguationData":[OSD([sQuery(id+"F0.wireOp",EDGE,"E11.2.0"),sQuery(id+"F0.wireOp",EDGE,"E11.2.1")])]});
            var Q9;
            Q9=makeQuery(id+"F5.opFillet","BLEND_EDGE",EDGE,{"blendedFrom":[makeQuery(id+"F1.opExtrude","SWEPT_EDGE",EDGE,{"disambiguationData":[OSD([sQuery(id+"F0.wireOp",EDGE,"E11.2.2"),sQuery(id+"F0.wireOp",EDGE,"E42.trimOffspring")])]}),makeQuery(id+"F1.opExtrude","SWEPT_FACE",FACE,{"disambiguationData":[OSD([sQuery(id+"F0.wireOp",EDGE,"E11.2.0")])]})],"blendedInto":[makeQuery(id+"F1.opExtrude","SWEPT_FACE",FACE,{"disambiguationData":[OSD([sQuery(id+"F0.wireOp",EDGE,"E11.2.0")])]})]});
            var Q10;
            Q10=makeQuery(id+"F5.opFillet","BLEND_EDGE",EDGE,{"blendedFrom":[makeQuery(id+"F1.opExtrude","SWEPT_EDGE",EDGE,{"disambiguationData":[OSD([sQuery(id+"F0.wireOp",EDGE,"E23.1.25"),sQuery(id+"F0.wireOp",EDGE,"E29.trimOffspring")])]}),makeQuery(id+"F1.opExtrude","SWEPT_FACE",FACE,{"disambiguationData":[OSD([sQuery(id+"F0.wireOp",EDGE,"E23.1.11")])]})],"blendedInto":[makeQuery(id+"F1.opExtrude","SWEPT_FACE",FACE,{"disambiguationData":[OSD([sQuery(id+"F0.wireOp",EDGE,"E23.1.11")])]})]});
            var Q11;
            Q11=makeQuery(id+"F1.opExtrude","SWEPT_EDGE",EDGE,{"disambiguationData":[OSD([sQuery(id+"F0.wireOp",EDGE,"E23.1.11"),sQuery(id+"F0.wireOp",EDGE,"E23.1.28")])]});
            var Q12;
            Q12=makeQuery(id+"F1.opExtrude","SWEPT_EDGE",EDGE,{"disambiguationData":[OSD([sQuery(id+"F0.wireOp",EDGE,"E23.1.12"),sQuery(id+"F0.wireOp",EDGE,"E23.1.19")])]});
            var Q13;
            Q13=makeQuery(id+"F1.opExtrude","SWEPT_EDGE",EDGE,{"disambiguationData":[OSD([sQuery(id+"F0.wireOp",EDGE,"E23.1.19"),sQuery(id+"F0.wireOp",EDGE,"E23.1.20")])]});
            var Q14;
            Q14=makeQuery(id+"F1.opExtrude","SWEPT_EDGE",EDGE,{"disambiguationData":[OSD([sQuery(id+"F0.wireOp",EDGE,"E23.1.16"),sQuery(id+"F0.wireOp",EDGE,"E23.1.17")])]});
            var Q15;
            Q15=makeQuery(id+"F1.opExtrude","SWEPT_EDGE",EDGE,{"disambiguationData":[OSD([sQuery(id+"F0.wireOp",EDGE,"E23.1.17"),sQuery(id+"F0.wireOp",EDGE,"E23.1.18")])]});
            var Q16;
            Q16=makeQuery(id+"F1.opExtrude","SWEPT_EDGE",EDGE,{"disambiguationData":[OSD([sQuery(id+"F0.wireOp",EDGE,"E23.1.14"),sQuery(id+"F0.wireOp",EDGE,"E23.1.24")])]});
            var Q17;
            Q17=makeQuery(id+"F1.opExtrude","SWEPT_EDGE",EDGE,{"disambiguationData":[OSD([sQuery(id+"F0.wireOp",EDGE,"E23.1.9"),sQuery(id+"F0.wireOp",EDGE,"E23.1.14")])]});
            var Q18;
            Q18=makeQuery(id+"F1.opExtrude","SWEPT_EDGE",EDGE,{"disambiguationData":[OSD([sQuery(id+"F0.wireOp",EDGE,"E23.1.23"),sQuery(id+"F0.wireOp",EDGE,"E23.1.27")])]});
            var Q19;
            Q19=makeQuery(id+"F5.opFillet","BLEND_EDGE",EDGE,{"blendedFrom":[makeQuery(id+"F1.opExtrude","SWEPT_EDGE",EDGE,{"disambiguationData":[OSD([sQuery(id+"F0.wireOp",EDGE,"E23.1.4"),sQuery(id+"F0.wireOp",EDGE,"E23.1.10")])]}),makeQuery(id+"F1.opExtrude","SWEPT_FACE",FACE,{"disambiguationData":[OSD([sQuery(id+"F0.wireOp",EDGE,"E23.1.23")])]})],"blendedInto":[makeQuery(id+"F1.opExtrude","SWEPT_FACE",FACE,{"disambiguationData":[OSD([sQuery(id+"F0.wireOp",EDGE,"E23.1.23")])]})]});
            var Q20;
            Q20=makeQuery(id+"F5.opFillet","BLEND_EDGE",EDGE,{"blendedFrom":[makeQuery(id+"F1.opExtrude","SWEPT_EDGE",EDGE,{"disambiguationData":[OSD([sQuery(id+"F0.wireOp",EDGE,"E23.2.25"),sQuery(id+"F0.wireOp",EDGE,"E46.trimOffspring")])]}),makeQuery(id+"F1.opExtrude","SWEPT_FACE",FACE,{"disambiguationData":[OSD([sQuery(id+"F0.wireOp",EDGE,"E23.2.11")])]})],"blendedInto":[makeQuery(id+"F1.opExtrude","SWEPT_FACE",FACE,{"disambiguationData":[OSD([sQuery(id+"F0.wireOp",EDGE,"E23.2.11")])]})]});
            var Q21;
            Q21=makeQuery(id+"F1.opExtrude","SWEPT_EDGE",EDGE,{"disambiguationData":[OSD([sQuery(id+"F0.wireOp",EDGE,"E23.2.11"),sQuery(id+"F0.wireOp",EDGE,"E23.2.28")])]});
            var Q22;
            Q22=makeQuery(id+"F1.opExtrude","SWEPT_EDGE",EDGE,{"disambiguationData":[OSD([sQuery(id+"F0.wireOp",EDGE,"E23.2.12"),sQuery(id+"F0.wireOp",EDGE,"E23.2.19")])]});
            var Q23;
            Q23=makeQuery(id+"F1.opExtrude","SWEPT_EDGE",EDGE,{"disambiguationData":[OSD([sQuery(id+"F0.wireOp",EDGE,"E23.2.19"),sQuery(id+"F0.wireOp",EDGE,"E23.2.20")])]});
            var Q24;
            Q24=makeQuery(id+"F1.opExtrude","SWEPT_EDGE",EDGE,{"disambiguationData":[OSD([sQuery(id+"F0.wireOp",EDGE,"E23.2.16"),sQuery(id+"F0.wireOp",EDGE,"E23.2.17")])]});
            var Q25;
            Q25=makeQuery(id+"F1.opExtrude","SWEPT_EDGE",EDGE,{"disambiguationData":[OSD([sQuery(id+"F0.wireOp",EDGE,"E23.2.17"),sQuery(id+"F0.wireOp",EDGE,"E23.2.18")])]});
            var Q26;
            Q26=makeQuery(id+"F1.opExtrude","SWEPT_EDGE",EDGE,{"disambiguationData":[OSD([sQuery(id+"F0.wireOp",EDGE,"E23.2.14"),sQuery(id+"F0.wireOp",EDGE,"E23.2.24")])]});
            var Q27;
            Q27=makeQuery(id+"F1.opExtrude","SWEPT_EDGE",EDGE,{"disambiguationData":[OSD([sQuery(id+"F0.wireOp",EDGE,"E23.2.9"),sQuery(id+"F0.wireOp",EDGE,"E23.2.14")])]});
            var Q28;
            Q28=makeQuery(id+"F1.opExtrude","SWEPT_EDGE",EDGE,{"disambiguationData":[OSD([sQuery(id+"F0.wireOp",EDGE,"E23.2.23"),sQuery(id+"F0.wireOp",EDGE,"E23.2.27")])]});
            var Q29;
            Q29=makeQuery(id+"F5.opFillet","BLEND_EDGE",EDGE,{"blendedFrom":[makeQuery(id+"F1.opExtrude","SWEPT_EDGE",EDGE,{"disambiguationData":[OSD([sQuery(id+"F0.wireOp",EDGE,"E23.2.4"),sQuery(id+"F0.wireOp",EDGE,"E23.2.10")])]}),makeQuery(id+"F1.opExtrude","SWEPT_FACE",FACE,{"disambiguationData":[OSD([sQuery(id+"F0.wireOp",EDGE,"E23.2.23")])]})],"blendedInto":[makeQuery(id+"F1.opExtrude","SWEPT_FACE",FACE,{"disambiguationData":[OSD([sQuery(id+"F0.wireOp",EDGE,"E23.2.23")])]})]});
            fillet(context, id + "F7", {"entities" : qUnion([Q0, Q1, Q2, Q3, Q4, Q5, Q6, Q7, Q8, Q9, Q10, Q11, Q12, Q13, Q14, Q15, Q16, Q17, Q18, Q19, Q20, Q21, Q22, Q23, Q24, Q25, Q26, Q27, Q28, Q29]), "radius" : 1 * mm, "tangentPropagation" : true, "allowEdgeOverflow" : false});
        }
        {
            var Q0;
            Q0=makeQuery(id+"F1.opExtrude","CAP_EDGE",EDGE,{"disambiguationData":[OSD([sQuery(id+"F0.wireOp",EDGE,"E41.1.0")])],"isStart":false});
            var Q1;
            Q1=makeQuery(id+"F1.opExtrude","CAP_EDGE",EDGE,{"disambiguationData":[OSD([sQuery(id+"F0.wireOp",EDGE,"E41.1.0")])],"isStart":true});
            chamfer(context, id + "F8", {"entities" : qUnion([Q0, Q1]), "width" : 1 * mm, "tangentPropagation" : true});
        }
    });
